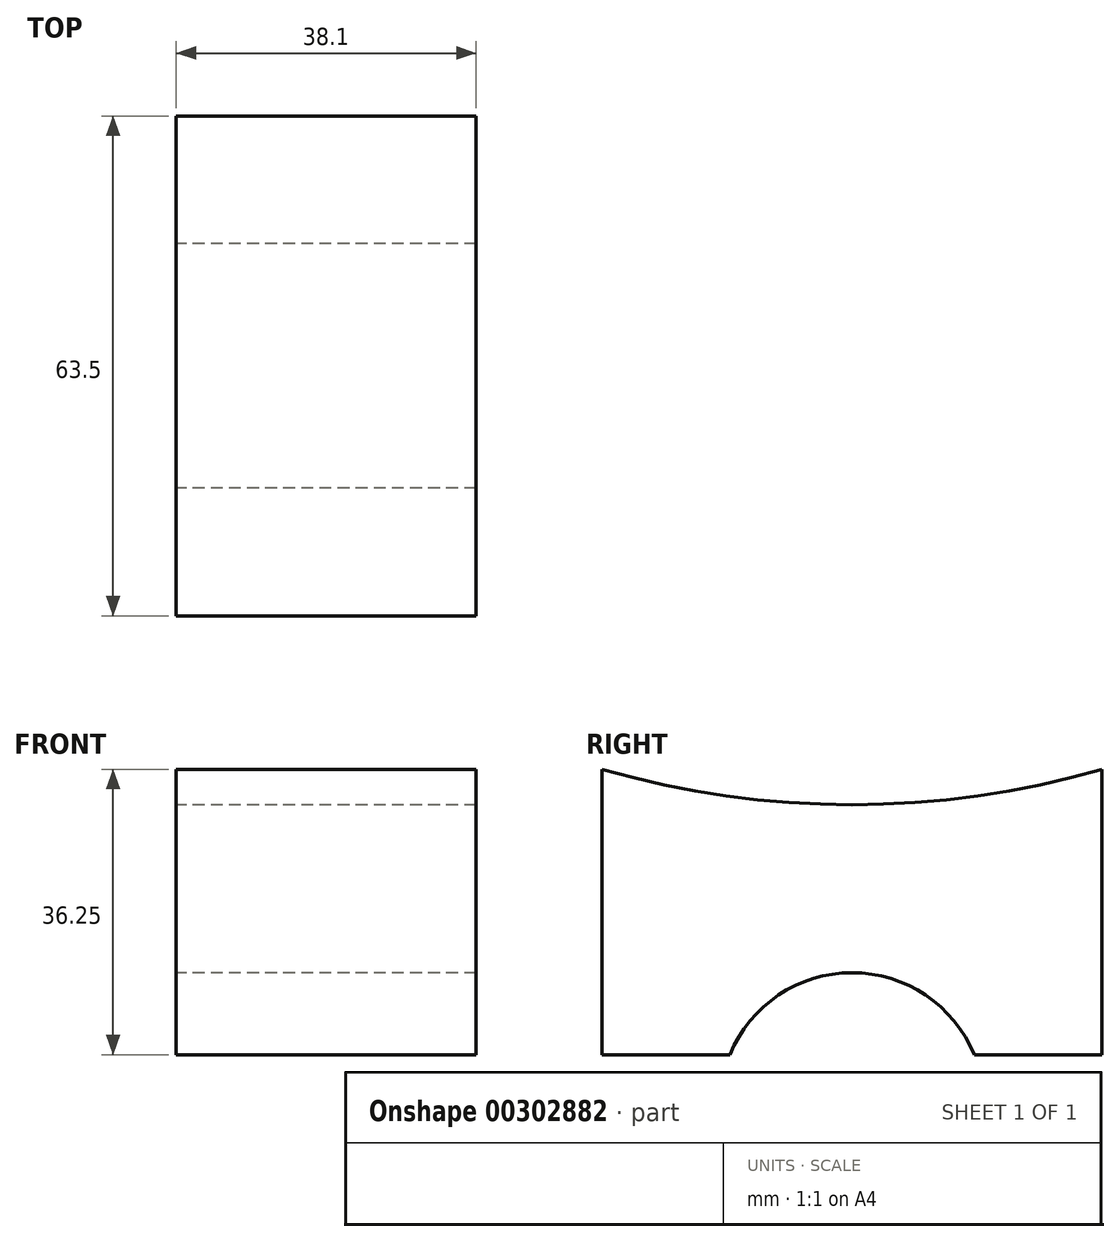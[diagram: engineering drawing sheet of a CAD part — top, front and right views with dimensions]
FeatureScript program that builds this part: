
annotation { "Feature Type Name" : "Feature", "Feature Type Description" : "" }
export const myFeature = defineFeature(function(context is Context, id is Id, definition is map)
    precondition{}
    {
        {
            var Q0;
            Q0=qCreatedBy(makeId("Right.planeOp"),FACE);
            var sketch = newSketch(context, id + "F0", { "sketchPlane" : qUnion([Q0])});
            skArc(sketch, "E0", {"start": v(15.51, -19.05) * mm, "mid": v(0, -8.64) * mm, "end": v(-15.51, -19.05) * mm});
            skArc(sketch, "E1", {"start": v(-31.75, 17.2) * mm, "mid": v(0, 12.7) * mm, "end": v(31.75, 17.2) * mm});
            skLineSegment(sketch, "E2", {"start": v(-31.75, 17.2) * mm, "end": v(-31.75, -19.05) * mm});
            skLineSegment(sketch, "E3", {"start": v(-31.75, -19.05) * mm, "end": v(-15.51, -19.05) * mm});
            skLineSegment(sketch, "E4", {"start": v(31.75, -19.05) * mm, "end": v(31.75, 17.2) * mm});
            skLineSegment(sketch, "E5.trimOffspring", {"start": v(15.51, -19.05) * mm, "end": v(31.75, -19.05) * mm});
            skSolve(sketch);
        }
        {
            var Q0;
            Q0 = qSketchRegion(id + "F0", true);
            extrude(context, id + "F1", {"entities" : qUnion([Q0]), "depth" : 19.05 * mm, "hasSecondDirection" : true, "secondDirectionOppositeDirection" : true, "secondDirectionDepth" : 19.05 * mm});
        }
    });
